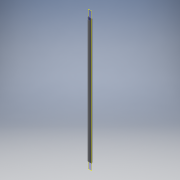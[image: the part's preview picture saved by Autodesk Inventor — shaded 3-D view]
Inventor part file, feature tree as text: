
AUTODESK INVENTOR PART (.ipt)
format: ipt  version: 2018 (Build 220112000, 112)  size: 113,664 bytes
history: native  units: mm
features: sketch x4, other x3, extrude x3, hole x1
ambient origin geometry x8: Origin, YZ Plane, XZ Plane, XY Plane, X Axis, Y Axis, Z Axis, Center Point
bodies: Body1 (feature_tree)
feature tree (11):
  other  "ソリッド1"
  extrude  "押し出し1"  Depth=27.2mm
  hole  "穴1"  [1 undecoded]
  other  "作業平面1"
  extrude  "押し出し3"  TaperAngle=0.0deg  [1 undecoded]
  extrude  "押し出し4"  Depth=27.2mm TaperAngle=0.0deg
  other  "作業平面2"
  sketch  "スケッチ1"
  sketch  "スケッチ3"
  sketch  "スケッチ4"
  sketch  "スケッチ5"
note: 2 required parameter values undecoded (feature->parameter linkage not recoverable at this tier; creation-order binding heuristic only, values carry confidence <= 0.55)
